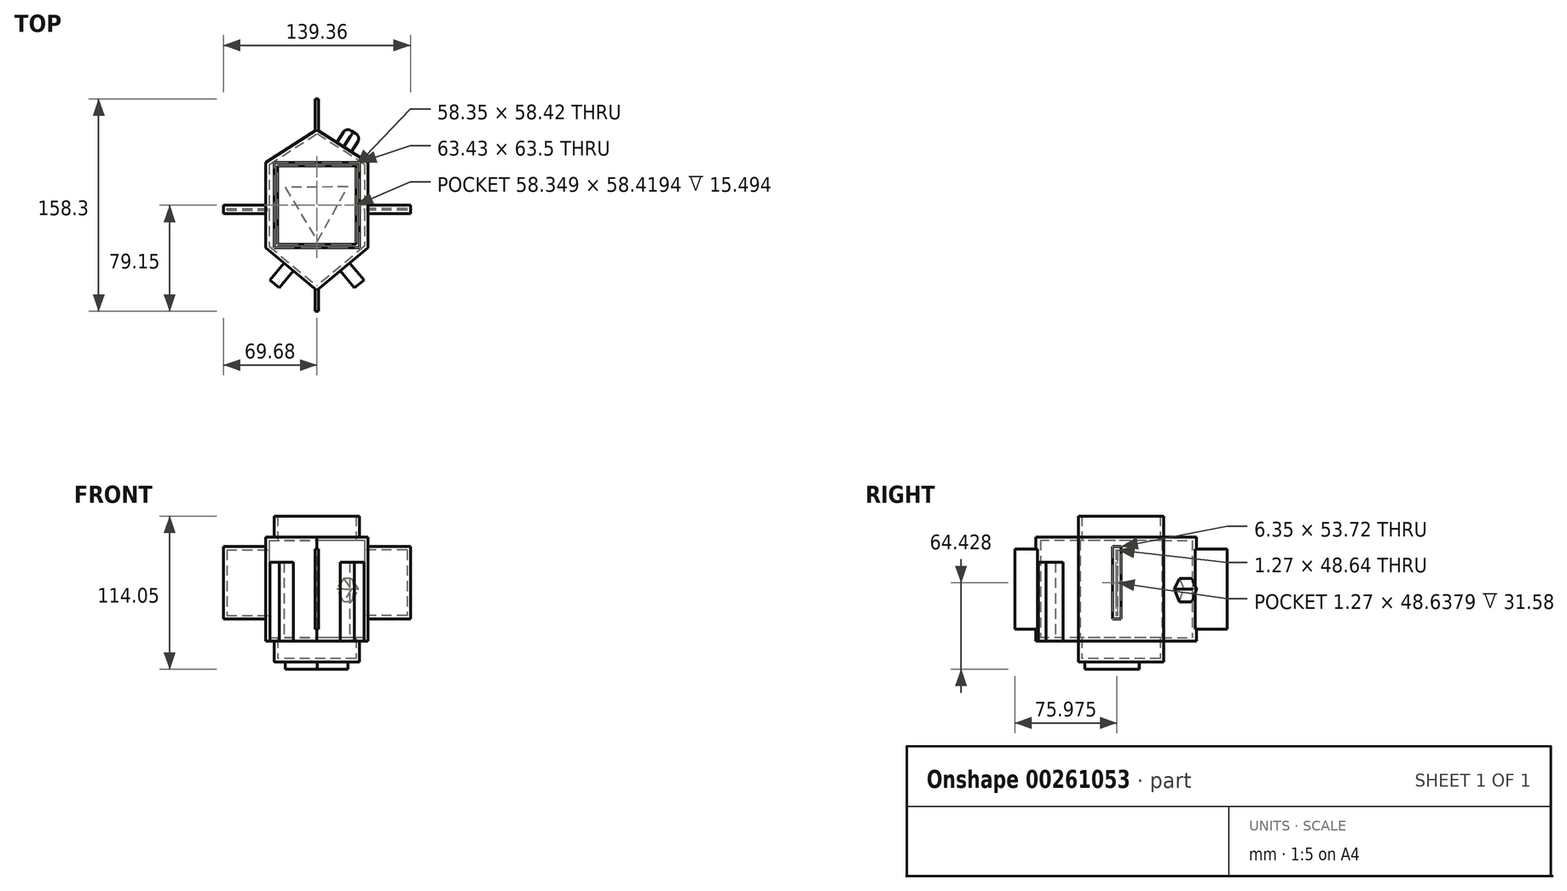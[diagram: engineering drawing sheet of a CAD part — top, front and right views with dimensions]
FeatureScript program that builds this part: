
annotation { "Feature Type Name" : "Feature", "Feature Type Description" : "" }
export const myFeature = defineFeature(function(context is Context, id is Id, definition is map)
    precondition{}
    {
        {
            var Q0;
            Q0=qCreatedBy(makeId("Top.planeOp"),FACE);
            var sketch = newSketch(context, id + "F0", { "sketchPlane" : qUnion([Q0])});
            skLineSegment(sketch, "E0.bottom", {"start": v(38.1, 31.75) * mm, "end": v(-38.1, 31.75) * mm});
            skLineSegment(sketch, "E0.top", {"start": v(38.1, -31.75) * mm, "end": v(-38.1, -31.75) * mm});
            skLineSegment(sketch, "E0.left", {"start": v(38.1, 31.75) * mm, "end": v(38.1, -31.75) * mm});
            skLineSegment(sketch, "E0.right", {"start": v(-38.1, 31.75) * mm, "end": v(-38.1, -31.75) * mm});
            skPoint(sketch, "E0.middle", {"position": v(0, 0) * mm});
            skLineSegment(sketch, "E1", {"start": v(-38.1, 31.75) * mm, "end": v(0, 56.22) * mm});
            skLineSegment(sketch, "E2", {"start": v(38.1, 31.75) * mm, "end": v(0, 56.22) * mm});
            skLineSegment(sketch, "E3", {"start": v(-38.1, -31.75) * mm, "end": v(0, -63.35) * mm});
            skLineSegment(sketch, "E4", {"start": v(38.1, -31.75) * mm, "end": v(0, -63.35) * mm});
            skLineSegment(sketch, "E5", {"start": v(-31.71, 31.75) * mm, "end": v(-31.71, -31.75) * mm});
            skPoint(sketch, "E6.MirrorCS.end.orphan", {"position": v(-25.33, -31.75) * mm});
            skPoint(sketch, "E6.MirrorCS.start.orphan", {"position": v(-25.33, 31.75) * mm});
            skPoint(sketch, "E7.MirrorCS.end.orphan", {"position": v(43.63, -31.75) * mm});
            skPoint(sketch, "E7.MirrorCS.start.orphan", {"position": v(43.91, 31.75) * mm});
            skLineSegment(sketch, "E8.MirrorCS", {"start": v(31.71, 31.75) * mm, "end": v(31.71, -31.75) * mm});
            skSolve(sketch);
        }
        {
            var Q0;
            Q0=qCreatedBy(makeId("Front.planeOp"),FACE);
            var sketch = newSketch(context, id + "F1", { "sketchPlane" : qUnion([Q0])});
            skLineSegment(sketch, "E9.bottom", {"start": v(69.68, 31.6) * mm, "end": v(29.45, 31.6) * mm});
            skLineSegment(sketch, "E9.top", {"start": v(69.68, -22.12) * mm, "end": v(29.45, -22.12) * mm});
            skLineSegment(sketch, "E9.left", {"start": v(69.68, 31.6) * mm, "end": v(69.68, -22.12) * mm});
            skLineSegment(sketch, "E9.right", {"start": v(29.45, 31.6) * mm, "end": v(29.45, -22.12) * mm});
            skLineSegment(sketch, "E10.MirrorCS", {"start": v(-69.68, 31.6) * mm, "end": v(-29.45, 31.6) * mm});
            skLineSegment(sketch, "E11.MirrorCS", {"start": v(-69.68, 31.6) * mm, "end": v(-69.68, -22.12) * mm});
            skLineSegment(sketch, "E12.MirrorCS", {"start": v(-69.68, -22.12) * mm, "end": v(-29.45, -22.12) * mm});
            skLineSegment(sketch, "E13.MirrorCS", {"start": v(-29.45, 31.6) * mm, "end": v(-29.45, -22.12) * mm});
            skSolve(sketch);
        }
        {
            var Q0;
            Q0=qCreatedBy(makeId("Right.planeOp"),FACE);
            var sketch = newSketch(context, id + "F2", { "sketchPlane" : qUnion([Q0])});
            skLineSegment(sketch, "E14", {"start": v(0, 0) * mm, "end": v(52.23, 0) * mm});
            skLineSegment(sketch, "E15.bottom", {"start": v(79.15, 29.88) * mm, "end": v(52.23, 29.88) * mm});
            skLineSegment(sketch, "E15.top", {"start": v(79.15, -29.88) * mm, "end": v(52.23, -29.88) * mm});
            skLineSegment(sketch, "E15.left", {"start": v(79.15, 29.88) * mm, "end": v(79.15, -29.88) * mm});
            skLineSegment(sketch, "E15.right", {"start": v(52.23, 29.88) * mm, "end": v(52.23, -29.88) * mm});
            skPoint(sketch, "E15.middle", {"position": v(65.69, 0) * mm});
            skLineSegment(sketch, "E16.MirrorCS", {"start": v(-79.15, 29.88) * mm, "end": v(-52.23, 29.88) * mm});
            skLineSegment(sketch, "E17.MirrorCS", {"start": v(-79.15, 29.88) * mm, "end": v(-79.15, -29.88) * mm});
            skLineSegment(sketch, "E18.MirrorCS", {"start": v(-52.23, 29.88) * mm, "end": v(-52.23, -29.88) * mm});
            skLineSegment(sketch, "E19.MirrorCS", {"start": v(-79.15, -29.88) * mm, "end": v(-52.23, -29.88) * mm});
            skLineSegment(sketch, "E20", {"start": v(0, 0) * mm, "end": v(-52.23, 0) * mm});
            skPoint(sketch, "E21.orphan", {"position": v(-79.15, 0) * mm});
            skSolve(sketch);
        }
        {
            var Q0;
            Q0=makeQuery(id+"F0.imprint","IMPRINT",FACE,{"disambiguationData":[TD([[makeQuery(id+"F0.imprint","IMPRINT",EDGE,{"derivedFrom":sQuery(id+"F0.wireOp",EDGE,"E0.bottom")}),-1.0]])]});
            var Q1;
            Q1=makeQuery(id+"F0.imprint","IMPRINT",FACE,{"disambiguationData":[TD([[makeQuery(id+"F0.imprint","IMPRINT",EDGE,{"derivedFrom":sQuery(id+"F0.wireOp",EDGE,"E0.top")}),1.0]])]});
            var Q2;
            {var subQ2=sQuery(id+"F0.wireOp",EDGE,"E5");Q2=makeQuery(id+"F0.imprint","IMPRINT",FACE,{"disambiguationData":[TD([[makeQuery(id+"F0.imprint","IMPRINT",EDGE,{"derivedFrom":subQ2}),-1.0]])]});}
            var Q3;
            {var subQ0=sQuery(id+"F0.wireOp",EDGE,"E0.left");Q3=makeQuery(id+"F0.imprint","IMPRINT",FACE,{"disambiguationData":[TD([[makeQuery(id+"F0.imprint","IMPRINT",EDGE,{"derivedFrom":subQ0}),-1.0]])]});}
            extrude(context, id + "F3", {"entities" : qUnion([Q0, Q1, Q2, Q3]), "endBound" : BoundingType.SYMMETRIC, "depth" : 77.72 * mm});
        }
        {
            var Q0;
            {var subQ0=sQuery(id+"F0.wireOp",EDGE,"E5");Q0=makeQuery(id+"F0.imprint","IMPRINT",FACE,{"disambiguationData":[TD([[makeQuery(id+"F0.imprint","IMPRINT",EDGE,{"derivedFrom":subQ0}),1.0]])]});}
            extrude(context, id + "F4", {"entities" : qUnion([Q0]), "operationType" : NewBodyOperationType.ADD, "endBound" : BoundingType.SYMMETRIC, "depth" : 108.7 * mm});
        }
        {
            var Q0;
            Q0 = qSketchRegion(id + "F2", true);
            extrude(context, id + "F5", {"entities" : qUnion([Q0]), "operationType" : NewBodyOperationType.ADD, "endBound" : BoundingType.SYMMETRIC, "oppositeDirection" : true, "depth" : 2.54 * mm});
        }
        {
            var Q0;
            Q0 = qSketchRegion(id + "F1", true);
            extrude(context, id + "F6", {"entities" : qUnion([Q0]), "operationType" : NewBodyOperationType.ADD, "depth" : 6.35 * mm});
        }
        {
            var Q0;
            Q0=makeQuery(id+"F4.opExtrude","CAP_FACE",FACE,{"disambiguationData":[OSD([sQuery(id+"F0.wireOp",EDGE,"E0.bottom"),sQuery(id+"F0.wireOp",EDGE,"E0.top"),sQuery(id+"F0.wireOp",EDGE,"E5"),sQuery(id+"F0.wireOp",EDGE,"921bfdc2-f642-4e1e-b524-79bdc1dc92150.MirrorCS")])],"isStart":false});
            shell(context, id + "F7", {"entities" : qUnion([Q0]), "thickness" : 2.54 * mm});
        }
        {
            var Q0;
            Q0=makeQuery(id+"F4.opExtrude","CAP_FACE",FACE,{"disambiguationData":[OSD([sQuery(id+"F0.wireOp",EDGE,"E0.bottom"),sQuery(id+"F0.wireOp",EDGE,"E0.top"),sQuery(id+"F0.wireOp",EDGE,"E5"),sQuery(id+"F0.wireOp",EDGE,"E8.MirrorCS")])],"isStart":true});
            var sketch = newSketch(context, id + "F8", { "sketchPlane" : qUnion([Q0])});
            skCircle(sketch, "E22.cCircle", {"center": v(0, 0) * mm, "radius": 13.44 * mm, "construction": true});
            skLineSegment(sketch, "E22.0", {"start": v(0.31, 26.87) * mm, "end": v(23.12, -13.7) * mm});
            skLineSegment(sketch, "E22.1", {"start": v(23.12, -13.7) * mm, "end": v(-23.43, -13.17) * mm});
            skLineSegment(sketch, "E22.2", {"start": v(-23.43, -13.17) * mm, "end": v(0.31, 26.87) * mm});
            skPoint(sketch, "E22.0.midPoint", {"position": v(11.71, 6.58) * mm});
            skSolve(sketch);
        }
        {
            var Q0;
            Q0=makeQuery(id+"F8.imprint","IMPRINT",FACE,{"disambiguationData":[TD([[makeQuery(id+"F8.imprint","IMPRINT",EDGE,{"derivedFrom":sQuery(id+"F8.wireOp",EDGE,"E22.0")}),-1.0]])]});
            extrude(context, id + "F9", {"entities" : qUnion([Q0]), "operationType" : NewBodyOperationType.ADD, "depth" : 5.33 * mm});
        }
        {
            var Q0;
            Q0=makeQuery(id+"F3.opExtrude","SWEPT_FACE",FACE,{"disambiguationData":[OSD([sQuery(id+"F0.wireOp",EDGE,"E2")])]});
            var sketch = newSketch(context, id + "F10", { "sketchPlane" : qUnion([Q0])});
            skLineSegment(sketch, "E23", {"start": v(6.67, 0) * mm, "end": v(6.67, 8.06) * mm});
            skPoint(sketch, "E23.startSnap0", {"position": v(28.87, 0) * mm});
            skLineSegment(sketch, "E24", {"start": v(6.67, 8.06) * mm, "end": v(0, 0) * mm});
            skLineSegment(sketch, "E25", {"start": v(6.67, 8.06) * mm, "end": v(12.8, 0) * mm});
            skLineSegment(sketch, "E26", {"start": v(0, 0) * mm, "end": v(6.67, -9.5) * mm});
            skLineSegment(sketch, "E27", {"start": v(6.67, -9.5) * mm, "end": v(6.67, 0) * mm});
            skLineSegment(sketch, "E28", {"start": v(6.67, -9.5) * mm, "end": v(12.8, 0) * mm});
            skSolve(sketch);
        }
        {
            var Q0;
            Q0=makeQuery(id+"F10.imprint","IMPRINT",FACE,{"disambiguationData":[TD([[makeQuery(id+"F10.imprint","IMPRINT",EDGE,{"derivedFrom":sQuery(id+"F10.wireOp",EDGE,"E23")}),1.0]])]});
            var Q1;
            Q1=makeQuery(id+"F10.imprint","IMPRINT",FACE,{"disambiguationData":[TD([[makeQuery(id+"F10.imprint","IMPRINT",EDGE,{"derivedFrom":sQuery(id+"F10.wireOp",EDGE,"E23")}),-1.0]])]});
            extrude(context, id + "F11", {"entities" : qUnion([Q0, Q1]), "operationType" : NewBodyOperationType.ADD, "depth" : 13.2 * mm});
        }
        {
            var Q0;
            Q0=makeQuery(id+"F11.opExtrude","CAP_EDGE",EDGE,{"disambiguationData":[OSD([sQuery(id+"F10.wireOp",EDGE,"E24")])],"isStart":false});
            var Q1;
            Q1=makeQuery(id+"F11.opExtrude","CAP_EDGE",EDGE,{"disambiguationData":[OSD([sQuery(id+"F10.wireOp",EDGE,"E28")])],"isStart":false});
            var Q2;
            Q2=makeQuery(id+"F11.opExtrude","CAP_EDGE",EDGE,{"disambiguationData":[OSD([sQuery(id+"F10.wireOp",EDGE,"E25")])],"isStart":false});
            var Q3;
            Q3=makeQuery(id+"F11.opExtrude","CAP_EDGE",EDGE,{"disambiguationData":[OSD([sQuery(id+"F10.wireOp",EDGE,"E26")])],"isStart":false});
            var Q4;
            Q4=makeQuery(id+"F6piugFjXTS1zHc_1.1.F11.opExtrude","CAP_FACE",FACE,{"disambiguationData":[OSD([sQuery(id+"F10.wireOp",EDGE,"E24"),sQuery(id+"F10.wireOp",EDGE,"E25"),sQuery(id+"F10.wireOp",EDGE,"E26"),sQuery(id+"F10.wireOp",EDGE,"E28")])],"isStart":false});
            fillet(context, id + "F12", {"entities" : qUnion([Q0, Q1, Q2, Q3, Q4]), "radius" : 3.68 * mm, "tangentPropagation" : true, "allowEdgeOverflow" : false});
        }
        {
            var Q0;
            Q0=makeQuery(id+"F3.opExtrude","SWEPT_FACE",FACE,{"disambiguationData":[OSD([sQuery(id+"F0.wireOp",EDGE,"E3")])]});
            var sketch = newSketch(context, id + "F13", { "sketchPlane" : qUnion([Q0])});
            skLineSegment(sketch, "E29.bottom", {"start": v(17.75, 19.85) * mm, "end": v(8.62, 19.85) * mm});
            skLineSegment(sketch, "E29.top", {"start": v(17.75, -38.87) * mm, "end": v(8.62, -38.87) * mm});
            skLineSegment(sketch, "E29.left", {"start": v(17.75, 19.85) * mm, "end": v(17.75, -38.87) * mm});
            skLineSegment(sketch, "E29.right", {"start": v(8.62, 19.85) * mm, "end": v(8.62, -38.87) * mm});
            skPoint(sketch, "E29.middle", {"position": v(13.18, -9.51) * mm});
            skSolve(sketch);
        }
        {
            var Q0;
            Q0 = qSketchRegion(id + "F13", true);
            extrude(context, id + "F14", {"entities" : qUnion([Q0]), "depth" : 16.5 * mm});
        }
        {
            var Q0;
            Q0=makeQuery(id+"F14.opExtrude","SWEPT_BODY",BODY,{"disambiguationData":[OSD([sQuery(id+"F13.wireOp",EDGE,"E29.bottom"),sQuery(id+"F13.wireOp",EDGE,"E29.top"),sQuery(id+"F13.wireOp",EDGE,"E29.left"),sQuery(id+"F13.wireOp",EDGE,"E29.right")])]});
            var Q1;
            Q1=qCreatedBy(makeId("Right.planeOp"),FACE);
            mirror(context, id + "F15", {"entities" : qUnion([Q0]), "mirrorPlane" : qUnion([Q1])});
        }
    });
